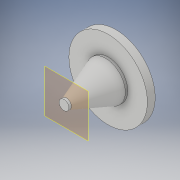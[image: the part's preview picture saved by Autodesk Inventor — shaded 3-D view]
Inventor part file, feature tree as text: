
AUTODESK INVENTOR PART (.ipt)
format: ipt  version: 2017 (Build 210142000, 142)  size: 121,344 bytes
history: native  units: in
note: dims shown in document units (in); Inventor stores cm internally (conversion verified against a paired STEP export)
features: sketch x4, extrude x3, other x2, plane x1, loft x1
ambient origin geometry x8: Origin, YZ Plane, XZ Plane, XY Plane, X Axis, Y Axis, Z Axis, Center Point
bodies: Solid1 (feature_tree)
feature tree (11):
  extrude  "Extrusion1"  Depth=0.0625in TaperAngle=0.0deg
  plane  "Work Plane1"
  extrude  "Extrusion2"  Depth=1.0in
  loft  "Loft1"
  extrude  "Extrusion3"  Depth=0.2in
  sketch  "Sketch5"  dims[d9=0.0in d10=90.0deg d11=2.0in d12=0.2in d13=0.0in]
  sketch  "Sketch1"  dims[d0=1.0in d1=0.0625in d2=0.0in]
  sketch  "Sketch2"  dims[d3=1.0in d4=0.25in]
  other  "Edges1"
  other  "Edges2"
  sketch  "Sketch3"  dims[d5=0.0625in d6=0.0in d7=0.0in d8=90.0deg]
